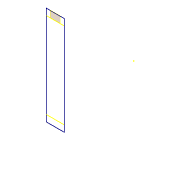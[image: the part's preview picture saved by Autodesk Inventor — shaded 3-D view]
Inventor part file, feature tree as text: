
AUTODESK INVENTOR PART (.ipt)
format: ipt  version: 2015 (Build 190159000, 159)  size: 70,656 bytes
history: native  units: in
note: dims shown in document units (in); Inventor stores cm internally (conversion verified against a paired STEP export)
features: plane x1, extrude x1, sketch x1
ambient origin geometry x8: Origin, YZ Plane, XZ Plane, XY Plane, X Axis, Y Axis, Z Axis, Center Point
bodies: Solid1 (feature_tree)
feature tree (3):
  plane  "Work Plane4"
  extrude  "Extrusion1"  [1 undecoded]
  sketch  "Sketch1"  dims[d0=0.0625in d1=0.0in]
note: 1 required parameter value undecoded (feature->parameter linkage not recoverable at this tier; creation-order binding heuristic only, values carry confidence <= 0.55)
